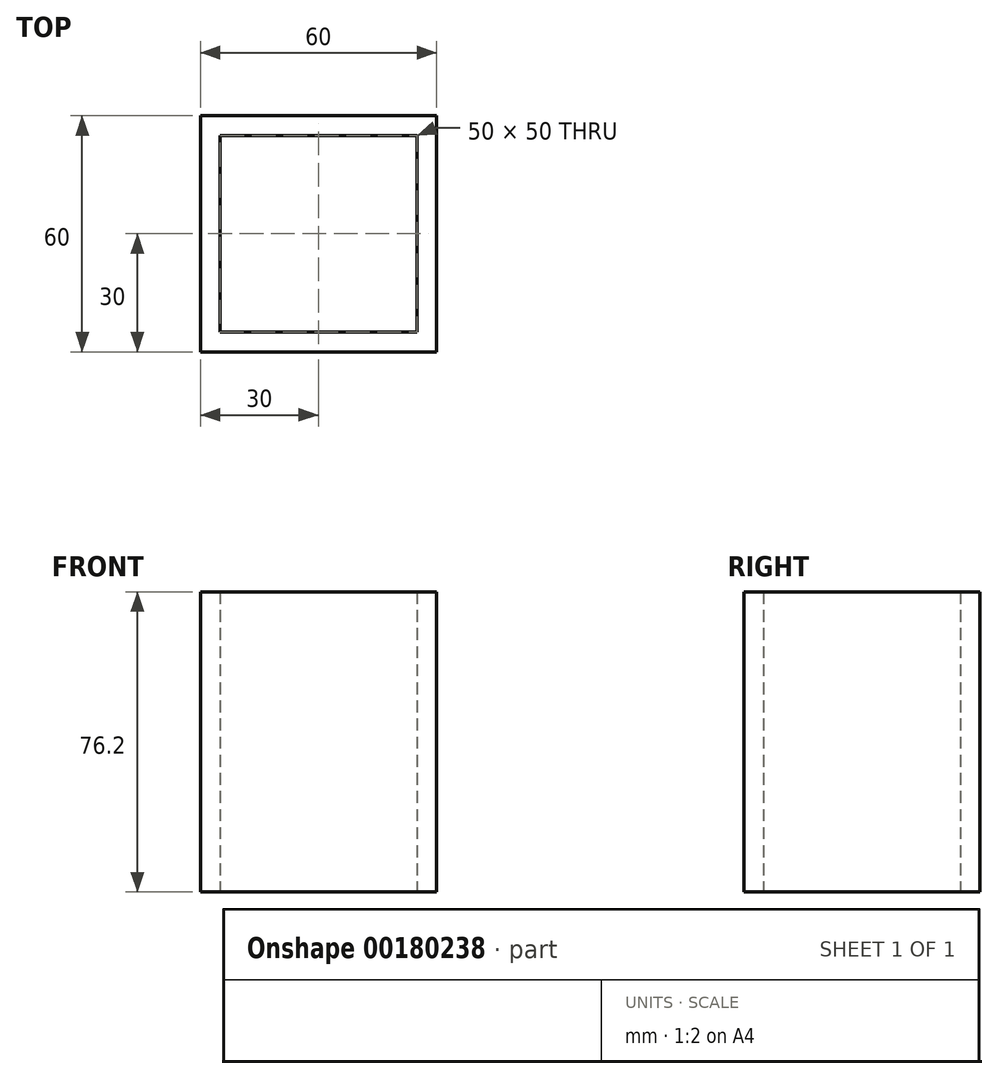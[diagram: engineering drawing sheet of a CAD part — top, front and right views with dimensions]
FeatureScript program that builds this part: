
annotation { "Feature Type Name" : "Feature", "Feature Type Description" : "" }
export const myFeature = defineFeature(function(context is Context, id is Id, definition is map)
    precondition{}
    {
        {
            var Q0;
            Q0=qCreatedBy(makeId("Top.planeOp"),FACE);
            var sketch = newSketch(context, id + "F0", { "sketchPlane" : qUnion([Q0])});
            skLineSegment(sketch, "E0.bottom", {"start": v(30, -30) * mm, "end": v(-30, -30) * mm});
            skLineSegment(sketch, "E0.top", {"start": v(30, 30) * mm, "end": v(-30, 30) * mm});
            skLineSegment(sketch, "E0.left", {"start": v(30, -30) * mm, "end": v(30, 30) * mm});
            skLineSegment(sketch, "E0.right", {"start": v(-30, -30) * mm, "end": v(-30, 30) * mm});
            skPoint(sketch, "E0.middle", {"position": v(0, 0) * mm});
            skLineSegment(sketch, "E1.0", {"start": v(25, 25) * mm, "end": v(-25, 25) * mm});
            skLineSegment(sketch, "E1.1", {"start": v(25, -25) * mm, "end": v(25, 25) * mm});
            skLineSegment(sketch, "E1.2", {"start": v(25, -25) * mm, "end": v(-25, -25) * mm});
            skLineSegment(sketch, "E1.3", {"start": v(-25, -25) * mm, "end": v(-25, 25) * mm});
            skSolve(sketch);
        }
        {
            var Q0;
            Q0=makeQuery(id+"F0.imprint","IMPRINT",FACE,{"disambiguationData":[TD([[makeQuery(id+"F0.imprint","IMPRINT",EDGE,{"derivedFrom":sQuery(id+"F0.wireOp",EDGE,"E0.bottom")}),-1.0]])]});
            extrude(context, id + "F1", {"entities" : qUnion([Q0]), "depth" : 76.2 * mm});
        }
    });
